# Revit family: Profile_Plastic-Components_Casing-Beads_Old-Style-Casing-Bead
name_source: partatom
category: Profiles
units: mm (PartAtom-declared; Revit-internal decimal feet)

## family parameters
Profile Usage = <Generic>
Rotate with component = No
Section Shape = Not Defined

## types (1)
- Profile_Plastic-Components_Casing-Beads_Old-Style-Casing-Bead
    A = 0' - 1 1/4"
    Assembly Code = C3020800
    B = 0' - 0 3/8"
    Construction Details = http://www.arcat.com
    Description = Trim-Tex Vinyl Drywall Accessory as Specified
    Expected Lifespan (Years) = 0
    Green Building-LEED = http://www.arcat.com
    Installation Phase = Stucco Underlayment
    Installation-Fabrication = http://www.plasticomponents.com
    Keynote = 09 22 36
    Maintenance Schedule (Months) = 0
    Manufacturer = Plastic Components, Inc.
    Manufacturer Fax = 305-887-2452
    Manufacturer Website = www.plasticcomponents.com
    Model = as Specified
    Product Data = http://www.arcat.com
    Product Properties = http://www.plasticomponents.com
    Sales Information = http://www.plasticomponents.com
    Specification = http://www.arcat.com
    Test Data = http://www.plasticomponents.com
    URL = www.plasticcomponents.com
    Warranty Duration (Years) = 0
